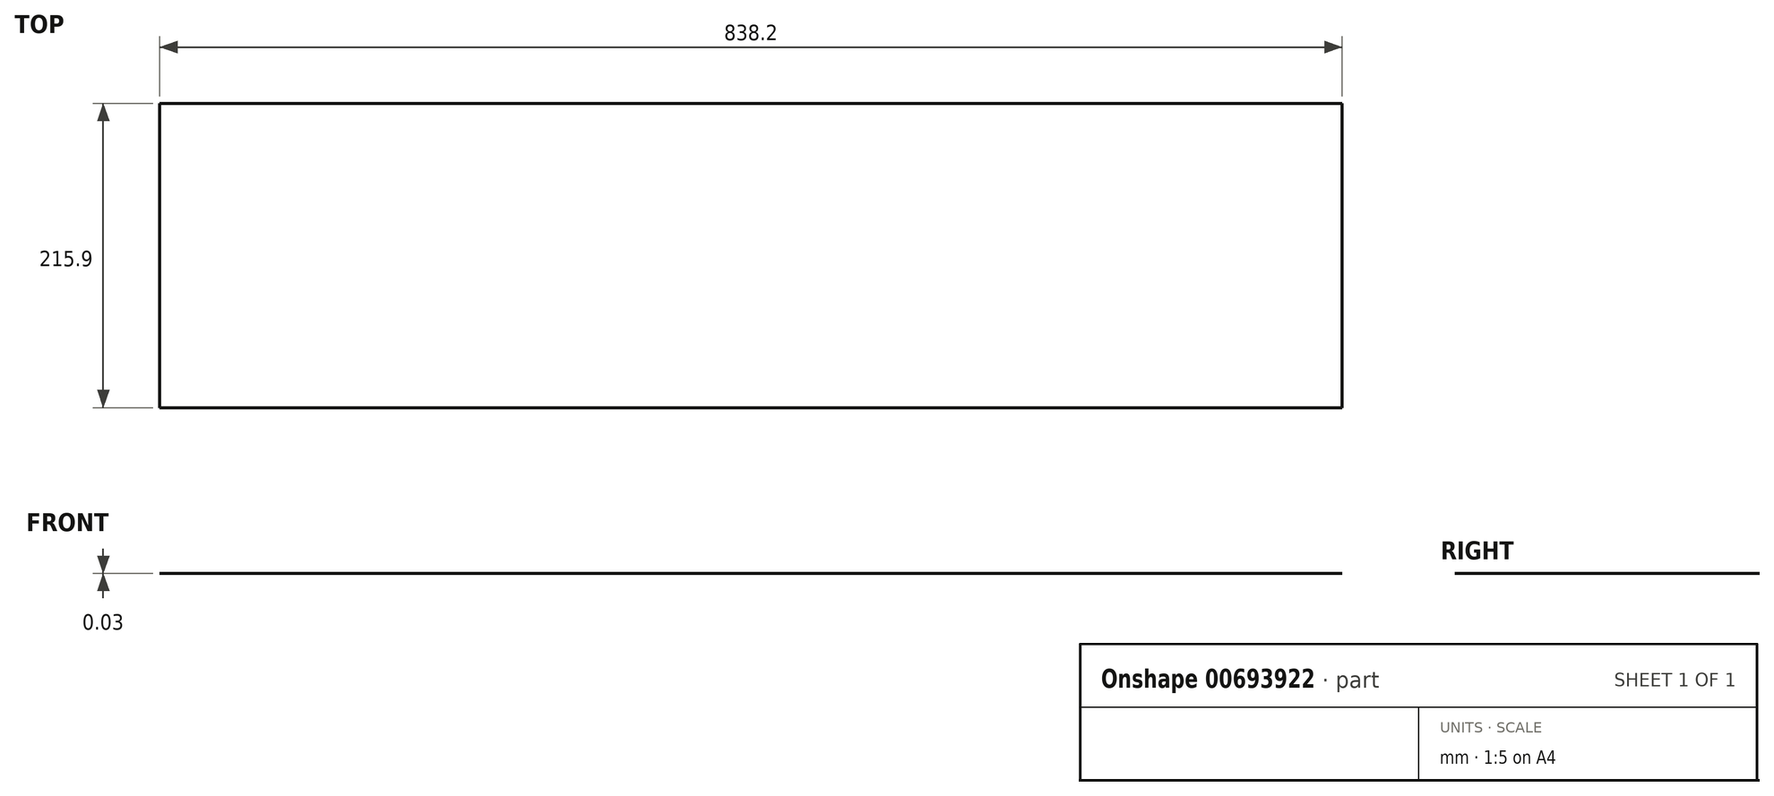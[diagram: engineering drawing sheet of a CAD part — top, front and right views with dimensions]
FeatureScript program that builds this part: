
annotation { "Feature Type Name" : "Feature", "Feature Type Description" : "" }
export const myFeature = defineFeature(function(context is Context, id is Id, definition is map)
    precondition{}
    {
        {
            var Q0;
            Q0=qCreatedBy(makeId("Top.planeOp"),FACE);
            var sketch = newSketch(context, id + "F0", { "sketchPlane" : qUnion([Q0])});
            skLineSegment(sketch, "E0.bottom", {"start": v(-419.1, 107.95) * mm, "end": v(419.1, 107.95) * mm});
            skLineSegment(sketch, "E0.top", {"start": v(-419.1, -107.95) * mm, "end": v(419.1, -107.95) * mm});
            skLineSegment(sketch, "E0.left", {"start": v(-419.1, 107.95) * mm, "end": v(-419.1, -107.95) * mm});
            skLineSegment(sketch, "E0.right", {"start": v(419.1, 107.95) * mm, "end": v(419.1, -107.95) * mm});
            skPoint(sketch, "E0.middle", {"position": v(0, 0) * mm});
            skSolve(sketch);
        }
        {
            var Q0;
            Q0=makeQuery(id+"F0.imprint","IMPRINT",FACE,{"disambiguationData":[TD([[makeQuery(id+"F0.imprint","IMPRINT",EDGE,{"derivedFrom":sQuery(id+"F0.wireOp",EDGE,"E0.bottom")}),-1.0]])]});
            extrude(context, id + "F1", {"entities" : qUnion([Q0]), "depth" : 3 / 101.6 * mm});
        }
    });
